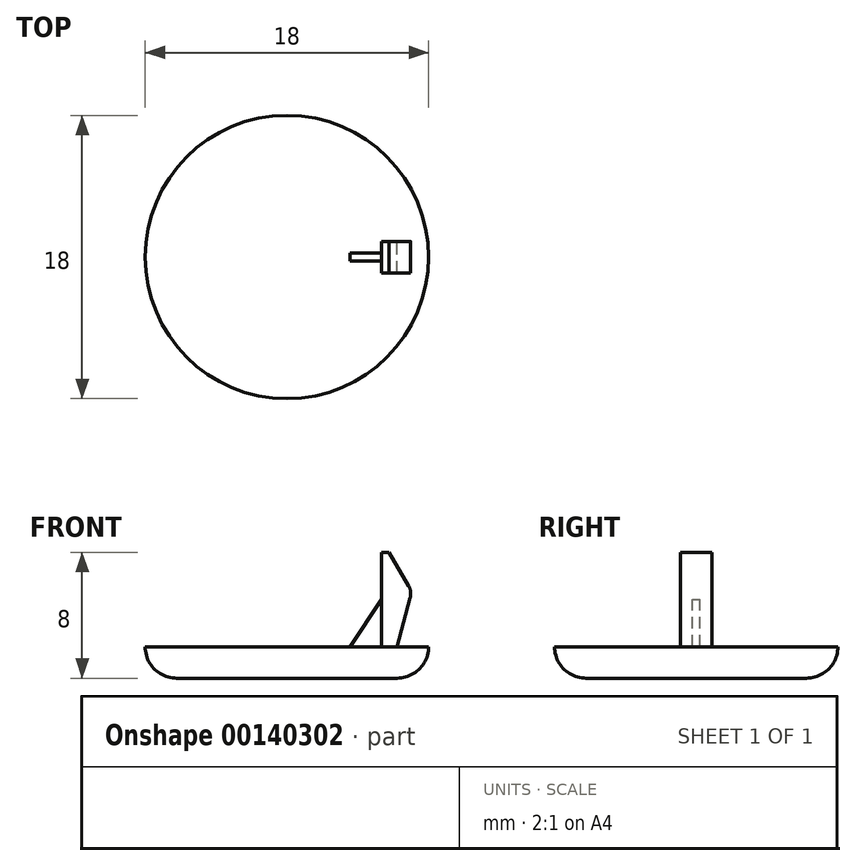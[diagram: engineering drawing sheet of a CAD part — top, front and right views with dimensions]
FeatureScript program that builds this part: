
annotation { "Feature Type Name" : "Feature", "Feature Type Description" : "" }
export const myFeature = defineFeature(function(context is Context, id is Id, definition is map)
    precondition{}
    {
        {
            var Q0;
            Q0=qCreatedBy(makeId("Front.planeOp"),FACE);
            var sketch = newSketch(context, id + "F0", { "sketchPlane" : qUnion([Q0])});
            skLineSegment(sketch, "E0", {"start": v(0, 0) * mm, "end": v(4, 0) * mm, "construction": true});
            skLineSegment(sketch, "E1", {"start": v(4, 0) * mm, "end": v(6, 0) * mm});
            skLineSegment(sketch, "E2", {"start": v(6, 0) * mm, "end": v(6, 6) * mm});
            skLineSegment(sketch, "E3", {"start": v(4, 0) * mm, "end": v(6, 3) * mm});
            skLineSegment(sketch, "E4", {"start": v(6, 6) * mm, "end": v(6.5, 6) * mm});
            skLineSegment(sketch, "E5", {"start": v(6, 0) * mm, "end": v(7, 0) * mm});
            skLineSegment(sketch, "E6", {"start": v(6.5, 6) * mm, "end": v(7.73, 3.87) * mm});
            skLineSegment(sketch, "E7", {"start": v(7, 0) * mm, "end": v(7.83, 3.1) * mm});
            skArc(sketch, "E8", {"start": v(7.83, 3.1) * mm, "mid": v(7.86, 3.5) * mm, "end": v(7.73, 3.87) * mm});
            skSolve(sketch);
        }
        {
            var Q0;
            {var subQ1=sQuery(id+"F0.wireOp",EDGE,"E4");Q0=makeQuery(id+"F0.imprint","IMPRINT",FACE,{"disambiguationData":[TD([[makeQuery(id+"F0.imprint","IMPRINT",EDGE,{"derivedFrom":subQ1}),-1.0]])]});}
            extrude(context, id + "F1", {"entities" : qUnion([Q0]), "endBound" : BoundingType.SYMMETRIC, "depth" : 2 * mm});
        }
        {
            var Q0;
            {var subQ0=sQuery(id+"F0.wireOp",EDGE,"E1");Q0=makeQuery(id+"F0.imprint","IMPRINT",FACE,{"disambiguationData":[TD([[makeQuery(id+"F0.imprint","IMPRINT",EDGE,{"derivedFrom":subQ0}),1.0]])]});}
            extrude(context, id + "F2", {"entities" : qUnion([Q0]), "operationType" : NewBodyOperationType.ADD, "endBound" : BoundingType.SYMMETRIC, "depth" : 0.5 * mm});
        }
        {
            var Q0;
            Q0=qCreatedBy(makeId("Top.planeOp"),FACE);
            var sketch = newSketch(context, id + "F3", { "sketchPlane" : qUnion([Q0])});
            skCircle(sketch, "E9", {"center": v(0, 0) * mm, "radius": 9 * mm});
            skSolve(sketch);
        }
        {
            var Q0;
            Q0=makeQuery(id+"F3.imprint","IMPRINT",FACE,{"disambiguationData":[TD([[makeQuery(id+"F3.imprint","IMPRINT",EDGE,{"derivedFrom":sQuery(id+"F3.wireOp",EDGE,"E9")}),1.0]])]});
            extrude(context, id + "F4", {"entities" : qUnion([Q0]), "operationType" : NewBodyOperationType.ADD, "oppositeDirection" : true, "depth" : 2 * mm});
        }
        {
            var Q0;
            Q0=makeQuery(id+"F4.opExtrude","CAP_EDGE",EDGE,{"disambiguationData":[OSD([sQuery(id+"F3.wireOp",EDGE,"E9")])],"isStart":false});
            fillet(context, id + "F5", {"entities" : qUnion([Q0]), "radius" : 2 * mm, "tangentPropagation" : true, "allowEdgeOverflow" : false});
        }
    });
